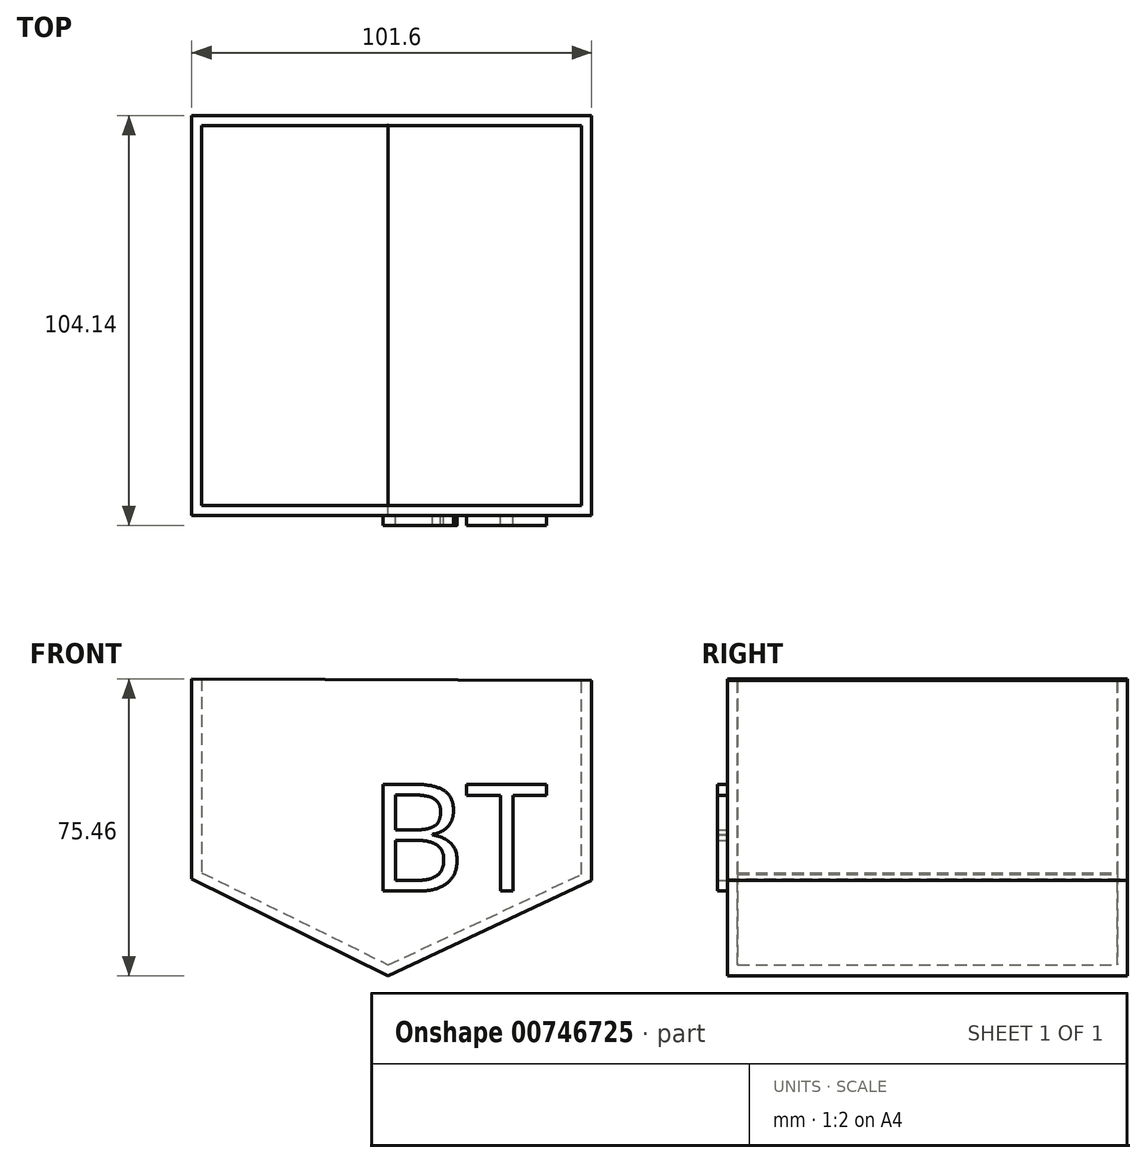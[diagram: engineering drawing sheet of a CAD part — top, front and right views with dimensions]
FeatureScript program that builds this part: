
annotation { "Feature Type Name" : "Feature", "Feature Type Description" : "" }
export const myFeature = defineFeature(function(context is Context, id is Id, definition is map)
    precondition{}
    {
        {
            var Q0;
            Q0=qCreatedBy(makeId("Front.planeOp"),FACE);
            var sketch = newSketch(context, id + "F0", { "sketchPlane" : qUnion([Q0])});
            skLineSegment(sketch, "E0", {"start": v(-49.88, 45.12) * mm, "end": v(-49.88, -5.68) * mm});
            skLineSegment(sketch, "E1", {"start": v(-49.88, -5.68) * mm, "end": v(0, -30.34) * mm});
            skLineSegment(sketch, "E2", {"start": v(0, -30.34) * mm, "end": v(51.72, -6.1) * mm});
            skLineSegment(sketch, "E3", {"start": v(51.72, -6.1) * mm, "end": v(51.72, 44.7) * mm});
            skLineSegment(sketch, "E4", {"start": v(51.72, 44.7) * mm, "end": v(-49.88, 45.12) * mm});
            skSolve(sketch);
        }
        {
            var Q0;
            Q0=makeQuery(id+"F0.imprint","IMPRINT",FACE,{"disambiguationData":[TD([[makeQuery(id+"F0.imprint","IMPRINT",EDGE,{"derivedFrom":sQuery(id+"F0.wireOp",EDGE,"E0")}),1.0]])]});
            extrude(context, id + "F1", {"entities" : qUnion([Q0]), "depth" : 101.6 * mm, "offsetDistance" : 25.4 * mm});
        }
        {
            var Q0;
            Q0=makeQuery(id+"F1.opExtrude","SWEPT_FACE",FACE,{"disambiguationData":[OSD([sQuery(id+"F0.wireOp",EDGE,"E4")])]});
            shell(context, id + "F2", {"entities" : qUnion([Q0]), "thickness" : 2.54 * mm});
        }
        {
            var Q0;
            Q0=makeQuery(id+"F1.opExtrude","CAP_FACE",FACE,{"disambiguationData":[OSD([sQuery(id+"F0.wireOp",EDGE,"E0"),sQuery(id+"F0.wireOp",EDGE,"E1"),sQuery(id+"F0.wireOp",EDGE,"E2"),sQuery(id+"F0.wireOp",EDGE,"E3"),sQuery(id+"F0.wireOp",EDGE,"E4")])],"isStart":false});
            var sketch = newSketch(context, id + "F3", { "sketchPlane" : qUnion([Q0])});
            skText(sketch, "E5", { "text": "BT", "fontName": "OpenSans-Regular.ttf"});
            const initialGuessF3  = {"E5": [-0.00502, -0.00874, 1, 0, 0.02735]};
            skSetInitialGuess(sketch, initialGuessF3);
            skSolve(sketch);
        }
        {
            var Q0;
            Q0 = qSketchRegion(id + "F3", true);
            extrude(context, id + "F4", {"entities" : qUnion([Q0]), "operationType" : NewBodyOperationType.ADD, "depth" : 2.54 * mm, "offsetDistance" : 25.4 * mm});
        }
    });
